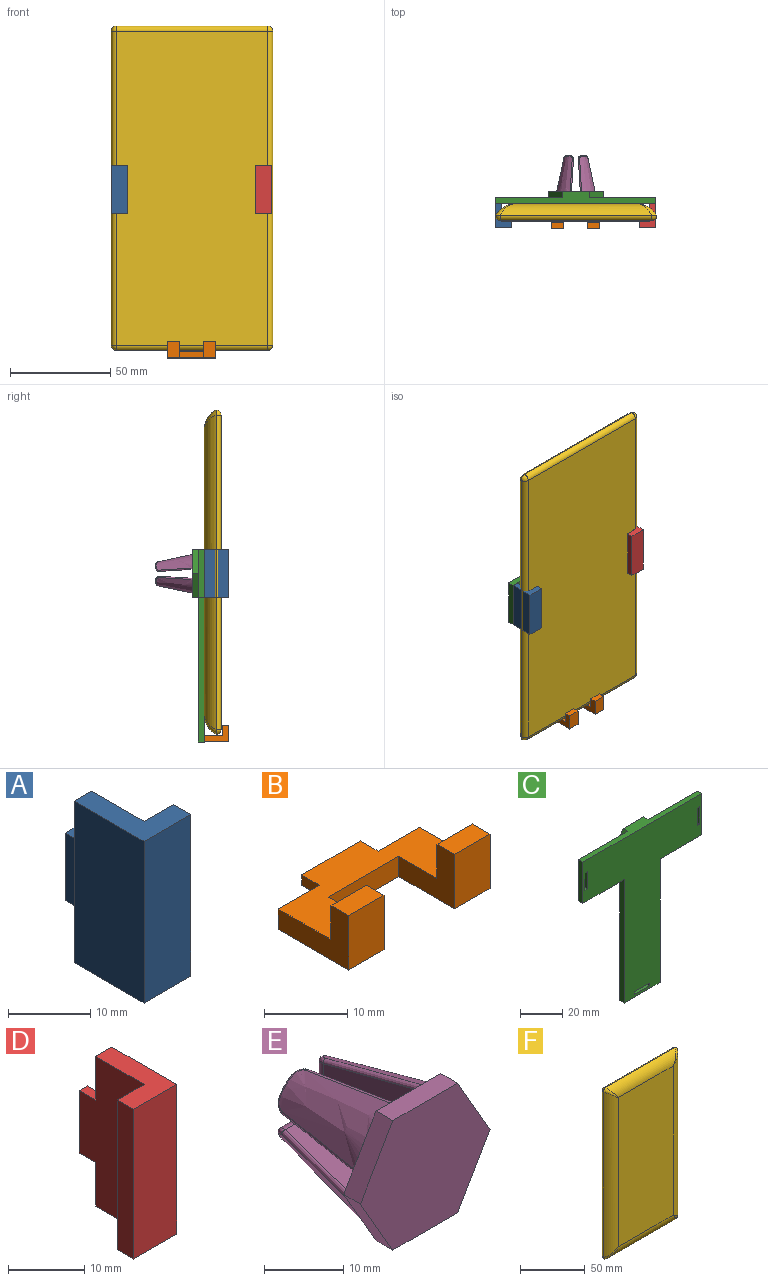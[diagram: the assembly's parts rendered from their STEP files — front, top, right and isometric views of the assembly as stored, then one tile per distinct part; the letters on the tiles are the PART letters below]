
ASSEMBLY  parts=6 mates=5
PART A: 12 faces, bbox 8x15x24 mm
  f0: plane 12x8mm, normal (0,0,-1), area 51mm2, adj f1,f4,f5,f6,f7,f11
  f1: plane 24x12mm, normal (1,0,0), area 246mm2, adj f0,f2,f3,f7,f8,f10,f11
  f2: plane 12x8mm, normal (0,0,1), area 51mm2, adj f1,f4,f5,f6,f7,f11
  f3: plane 10x1.5mm, normal (0,1,0), area 15mm2, adj f1,f8,f9,f10
  f4: plane 24x12mm, normal (-1,0,0), area 288mm2, adj f0,f2,f6,f11
  f5: plane 24x3mm, normal (1,0,0), area 72mm2, adj f0,f2,f6,f7
  f6: plane 24x8mm, normal (0,-1,0), area 192mm2, adj f0,f2,f4,f5
  f7: plane 24x5mm, normal (0,1,0), area 120mm2, adj f0,f1,f2,f5
  f8: plane 3x1.5mm, normal (0,0,1), area 4.5mm2, adj f1,f3,f9,f11
  f9: plane 10x3mm, normal (-1,0,0), area 30mm2, adj f3,f8,f10,f11
  f10: plane 3x1.5mm, normal (0,0,-1), area 4.5mm2, adj f1,f3,f9,f11
  f11: plane 24x3mm, normal (0,1,0), area 57mm2, adj f0,f1,f2,f4,f8,f9,f10
PART B: 18 faces, bbox 24x15x8 mm
  f0: plane 10x1.5mm, normal (0,1,0), area 15mm2, adj f1,f2,f3,f4
  f1: plane 24x12mm, normal (0,0,1), area 168mm2, adj f0,f3,f4,f5,f6,f7,f9,f12
  f2: plane 10x3mm, normal (0,0,-1), area 30mm2, adj f0,f3,f4,f5
  f3: plane 3x1.5mm, normal (-1,0,0), area 4.5mm2, adj f0,f1,f2,f5
  f4: plane 3x1.5mm, normal (1,0,0), area 4.5mm2, adj f0,f1,f2,f5
  f5: plane 24x3mm, normal (0,1,0), area 57mm2, adj f1,f2,f3,f4,f7,f8,f16
  f6: plane 9.5x8mm, normal (1,0,0), area 43.5mm2, adj f1,f8,f9,f10,f11,f17
  f7: plane 12x8mm, normal (-1,0,0), area 51mm2, adj f1,f5,f8,f9,f10,f11
  f8: plane 24x12mm, normal (0,0,-1), area 174mm2, adj f5,f6,f7,f11,f12,f15,f16,f17
  f9: plane 6x5mm, normal (0,1,0), area 30mm2, adj f1,f6,f7,f10
  f10: plane 6x3mm, normal (0,0,1), area 18mm2, adj f6,f7,f9,f11
  f11: plane 8x6mm, normal (0,-1,0), area 48mm2, adj f6,f7,f8,f10
  f12: plane 9.5x8mm, normal (-1,0,0), area 43.5mm2, adj f1,f8,f13,f14,f15,f17
  f13: plane 6x5mm, normal (0,1,0), area 30mm2, adj f1,f12,f14,f16
  f14: plane 6x3mm, normal (0,0,1), area 18mm2, adj f12,f13,f15,f16
  f15: plane 8x6mm, normal (0,-1,0), area 48mm2, adj f8,f12,f14,f16
  f16: plane 12x8mm, normal (1,0,0), area 51mm2, adj f1,f5,f8,f13,f14,f15
  f17: plane 12x3mm, normal (0,-1,0), area 36mm2, adj f1,f6,f8,f12
PART C: 35 faces, bbox 80x6x96 mm
  f0: plane 72x3mm, normal (-1,0,0), area 216mm2, adj f2,f3,f4,f5
  f1: plane 72x3mm, normal (1,0,0), area 216mm2, adj f2,f3,f4,f6
  f2: plane 24x3mm, normal (0,0,-1), area 72mm2, adj f0,f1,f3,f4
  f3: plane 96x80mm, normal (0,1,0), area 3100.7mm2, adj f0,f1,f2,f5,f6,f7,f8,f9
  f4: plane 96x80mm, normal (0,-1,0), area 3599.5mm2, adj f0,f1,f2,f5,f6,f7,f8,f9
  f5: plane 28x3mm, normal (0,0,-1), area 84mm2, adj f0,f3,f4,f9
  f6: plane 28x3mm, normal (0,0,-1), area 84mm2, adj f1,f3,f4,f7
  f7: plane 24x3mm, normal (1,0,0), area 72mm2, adj f3,f4,f6,f8
  f8: plane 80x6mm, normal (0,0,1), area 281.6mm2, adj f3,f4,f7,f9,f16,f17,f21
  f9: plane 24x3mm, normal (-1,0,0), area 72mm2, adj f3,f4,f5,f8
  f10: plane 10.1x5.83mm, normal (0.87,0,-0.5), area 35mm2, adj f11,f20,f21,f22
  f11: plane 10.1x5.83mm, normal (0.87,0,0.5), area 35mm2, adj f10,f12,f21,f22
  f12: plane 11.66x3mm, normal (0,0,1), area 35mm2, adj f11,f13,f21,f22
  f13: plane 10.1x5.83mm, normal (-0.87,0,0.5), area 35mm2, adj f12,f14,f21,f22
  f14: plane 10.1x5.83mm, normal (-0.87,0,-0.5), area 35mm2, adj f13,f20,f21,f22
  f15: plane 12x6.93mm, normal (-0.87,0,-0.5), area 41.6mm2, adj f3,f16,f19,f21
  f16: plane 12x6.93mm, normal (-0.87,0,0.5), area 41.6mm2, adj f3,f8,f15,f21
  f17: plane 12x6.93mm, normal (0.87,0,0.5), area 41.6mm2, adj f3,f8,f18,f21
  f18: plane 12x6.93mm, normal (0.87,0,-0.5), area 41.6mm2, adj f3,f17,f19,f21
  f19: plane 13.86x3mm, normal (0,0,-1), area 41.6mm2, adj f3,f15,f18,f21
  f20: plane 11.66x3mm, normal (0,0,-1), area 35mm2, adj f10,f14,f21,f22
  f21: plane 27.71x24mm, normal (0,1,0), area 145.5mm2, adj f8,f10,f11,f12,f13,f14,f15,f16
  f22: plane 23.33x20.2mm, normal (0,1,0), area 353.4mm2, adj f10,f11,f12,f13,f14,f20
  f23: plane 10.1x3mm, normal (1,0,0), area 30.3mm2, adj f3,f4,f24,f25
  f24: plane 3x1.6mm, normal (0,0,-1), area 4.8mm2, adj f3,f4,f23,f26
  f25: plane 3x1.6mm, normal (0,0,1), area 4.8mm2, adj f3,f4,f23,f26
  f26: plane 10.1x3mm, normal (-1,0,0), area 30.3mm2, adj f3,f4,f24,f25
  f27: plane 10.1x3mm, normal (0,0,1), area 30.3mm2, adj f3,f4,f28,f29
  f28: plane 3x1.6mm, normal (1,0,0), area 4.8mm2, adj f3,f4,f27,f30
  f29: plane 3x1.6mm, normal (-1,0,0), area 4.8mm2, adj f3,f4,f27,f30
  f30: plane 10.1x3mm, normal (0,0,-1), area 30.3mm2, adj f3,f4,f28,f29
  f31: plane 10.1x3mm, normal (1,0,0), area 30.3mm2, adj f3,f4,f32,f33
  f32: plane 3x1.6mm, normal (0,0,-1), area 4.8mm2, adj f3,f4,f31,f34
  f33: plane 3x1.6mm, normal (0,0,1), area 4.8mm2, adj f3,f4,f31,f34
  f34: plane 10.1x3mm, normal (-1,0,0), area 30.3mm2, adj f3,f4,f32,f33
PART D: 12 faces, bbox 8x15x24 mm
  f0: plane 12x8mm, normal (0,0,-1), area 51mm2, adj f1,f3,f5,f6,f7,f11
  f1: plane 24x12mm, normal (1,0,0), area 288mm2, adj f0,f4,f6,f11
  f2: plane 10x1.5mm, normal (0,1,0), area 15mm2, adj f3,f8,f9,f10
  f3: plane 24x12mm, normal (-1,0,0), area 246mm2, adj f0,f2,f4,f7,f8,f10,f11
  f4: plane 12x8mm, normal (0,0,1), area 51mm2, adj f1,f3,f5,f6,f7,f11
  f5: plane 24x3mm, normal (-1,0,0), area 72mm2, adj f0,f4,f6,f7
  f6: plane 24x8mm, normal (0,-1,0), area 192mm2, adj f0,f1,f4,f5
  f7: plane 24x5mm, normal (0,1,0), area 120mm2, adj f0,f3,f4,f5
  f8: plane 3x1.5mm, normal (0,0,-1), area 4.5mm2, adj f2,f3,f9,f11
  f9: plane 10x3mm, normal (1,0,0), area 30mm2, adj f2,f8,f10,f11
  f10: plane 3x1.5mm, normal (0,0,1), area 4.5mm2, adj f2,f3,f9,f11
  f11: plane 24x3mm, normal (0,1,0), area 57mm2, adj f0,f1,f3,f4,f8,f9,f10
PART E: 60 faces, bbox 23.2x23.4x20.6 mm
  f0: bspline ~17.61x8.03mm, area 141.2mm2, adj f4,f18,f19,f20,f48,f52
  f1: bspline ~17.61x8.03mm, area 141.2mm2, adj f4,f22,f23,f24,f43,f47
  f2: bspline ~17.61x8.03mm, area 141.2mm2, adj f4,f26,f27,f28,f38,f42
  f3: bspline ~17.61x8.03mm, area 141.2mm2, adj f4,f30,f31,f32,f33,f37
  f4: plane 23.16x20.06mm, normal (0,1,0), area 188.5mm2, adj f0,f1,f2,f3,f6,f7,f9,f10
  f5: plane 2.21x2.21mm, normal (0,1,0), area 2.9mm2, adj f31,f34,f36
  f6: plane 16.41x7.38mm, normal (-1,-0.06,0), area 84.4mm2, adj f4,f29,f32,f34
  f7: plane 16.41x7.38mm, normal (0,-0.06,-1), area 84.4mm2, adj f4,f29,f30,f36
  f8: plane 2.21x2.21mm, normal (0,1,0), area 2.9mm2, adj f27,f39,f41
  f9: plane 16.41x7.38mm, normal (1,-0.06,0), area 84.4mm2, adj f4,f25,f28,f39
  f10: plane 16.41x7.38mm, normal (0,-0.06,-1), area 84.4mm2, adj f4,f25,f26,f41
  f11: plane 2.21x2.21mm, normal (0,1,0), area 2.9mm2, adj f23,f44,f46
  f12: plane 16.41x7.38mm, normal (-1,-0.06,0), area 84.4mm2, adj f4,f21,f24,f44
  f13: plane 16.41x7.38mm, normal (0,-0.06,1), area 84.4mm2, adj f4,f21,f22,f46
  f14: plane 2.21x2.21mm, normal (0,1,0), area 2.9mm2, adj f19,f49,f51
  f15: plane 16.41x7.38mm, normal (0,-0.06,1), area 84.4mm2, adj f4,f17,f20,f49
  f16: plane 16.41x7.38mm, normal (1,-0.06,0), area 84.4mm2, adj f4,f17,f18,f51
  f17: cylinder r=0.5mm len=16.42mm, axis (-0.06,-1,-0.06), area 12.9mm2, adj f4,f15,f16,f50
  f18: bspline ~22.76x5.5mm, area 15.8mm2, adj f0,f4,f16,f52
  f19: bspline ~3.66x3.46mm, area 2.2mm2, adj f0,f14,f48,f52
  f20: bspline ~22.76x5.5mm, area 15.8mm2, adj f0,f4,f15,f48
  f21: cylinder r=0.5mm len=16.42mm, axis (0.06,-1,-0.06), area 12.9mm2, adj f4,f12,f13,f45
  f22: bspline ~22.76x5.5mm, area 15.8mm2, adj f1,f4,f13,f47
  f23: bspline ~3.66x3.46mm, area 2.2mm2, adj f1,f11,f43,f47
  f24: bspline ~22.76x5.5mm, area 15.8mm2, adj f1,f4,f12,f43
  f25: cylinder r=0.5mm len=16.42mm, axis (-0.06,-1,0.06), area 12.9mm2, adj f4,f9,f10,f40
  f26: bspline ~22.76x5.5mm, area 15.8mm2, adj f2,f4,f10,f42
  f27: bspline ~3.66x3.46mm, area 2.2mm2, adj f2,f8,f38,f42
  f28: bspline ~22.76x5.5mm, area 15.8mm2, adj f2,f4,f9,f38
  f29: cylinder r=0.5mm len=16.42mm, axis (-0.06,1,-0.06), area 12.9mm2, adj f4,f6,f7,f35
  f30: bspline ~20.19x4.95mm, area 15.8mm2, adj f3,f4,f7,f37
  f31: bspline ~3.66x3.46mm, area 2.2mm2, adj f3,f5,f33,f37
  f32: bspline ~20.19x4.95mm, area 15.8mm2, adj f3,f4,f6,f33
  f33: bspline ~2.04x1.76mm, area 1.9mm2, adj f3,f31,f32,f34
  f34: cylinder r=1.5mm len=3.87mm, axis (0,0,-1), area 7.4mm2, adj f5,f6,f33,f35
  f35: bspline ~1.76x1.5mm, area 0.9mm2, adj f29,f34,f36
  f36: cylinder r=1.5mm len=3.87mm, axis (-1,0,0), area 7.4mm2, adj f5,f7,f35,f37
  f37: bspline ~1.92x1.83mm, area 1.9mm2, adj f3,f30,f31,f36
  f38: bspline ~1.92x1.83mm, area 1.9mm2, adj f2,f27,f28,f39
  f39: cylinder r=1.5mm len=3.87mm, axis (0,0,-1), area 7.4mm2, adj f8,f9,f38,f40
  f40: bspline ~1.76x1.5mm, area 0.9mm2, adj f25,f39,f41
  f41: cylinder r=1.5mm len=3.87mm, axis (1,0,0), area 7.4mm2, adj f8,f10,f40,f42
  f42: bspline ~2.04x1.76mm, area 1.9mm2, adj f2,f26,f27,f41
  f43: bspline ~1.92x1.83mm, area 1.9mm2, adj f1,f23,f24,f44
  f44: cylinder r=1.5mm len=3.87mm, axis (0,0,1), area 7.4mm2, adj f11,f12,f43,f45
  f45: bspline ~1.76x1.5mm, area 0.9mm2, adj f21,f44,f46
  f46: cylinder r=1.5mm len=3.87mm, axis (-1,0,0), area 7.4mm2, adj f11,f13,f45,f47
  f47: bspline ~2.04x1.76mm, area 1.9mm2, adj f1,f22,f23,f46
  f48: bspline ~1.92x1.83mm, area 1.9mm2, adj f0,f19,f20,f49
  f49: cylinder r=1.5mm len=3.87mm, axis (1,0,0), area 7.4mm2, adj f14,f15,f48,f50
  f50: bspline ~1.76x1.5mm, area 0.9mm2, adj f17,f49,f51
  f51: cylinder r=1.5mm len=3.87mm, axis (0,0,1), area 7.4mm2, adj f14,f16,f50,f52
  f52: bspline ~2.04x1.76mm, area 1.9mm2, adj f0,f18,f19,f51
  f53: plane 11.55x3mm, normal (0,0,1), area 34.6mm2, adj f4,f54,f58,f59
  f54: plane 10x5.77mm, normal (0.87,0,0.5), area 34.6mm2, adj f4,f53,f55,f59
  f55: plane 10x5.77mm, normal (0.87,0,-0.5), area 34.6mm2, adj f4,f54,f56,f59
  f56: plane 11.55x3mm, normal (0,0,-1), area 34.6mm2, adj f4,f55,f57,f59
  f57: plane 10x5.77mm, normal (-0.87,0,-0.5), area 34.6mm2, adj f4,f56,f58,f59
  f58: plane 10x5.77mm, normal (-0.87,0,0.5), area 34.6mm2, adj f4,f53,f57,f59
  f59: plane 23.09x20mm, normal (0,-1,0), area 346.4mm2, adj f53,f54,f55,f56,f57,f58
PART F: 18 faces, bbox 80.6x8.5x162 mm
  f0: plane 141.22x59.82mm, normal (0,-1,0), area 8446.9mm2, adj f10,f13,f14,f17
  f1: plane 157x75.6mm, normal (0,1,0), area 11869.2mm2, adj f3,f4,f7,f8
  f2: sphere r=2.5mm, area 9.8mm2, adj f3,f4,f11
  f3: cylinder r=2.5mm len=75.6mm, axis (-1,0,0), area 296.9mm2, adj f1,f2,f5,f13
  f4: cylinder r=2.5mm len=157mm, axis (0,0,-1), area 616.5mm2, adj f1,f2,f6,f10
  f5: sphere r=2.5mm, area 13.4mm2, adj f3,f7,f15
  f6: sphere r=2.5mm, area 9.8mm2, adj f4,f8,f12
  f7: cylinder r=2.5mm len=157mm, axis (0,0,1), area 616.5mm2, adj f1,f5,f9,f17
  f8: cylinder r=2.5mm len=75.6mm, axis (1,0,0), area 296.9mm2, adj f1,f6,f9,f14
  f9: sphere r=2.5mm, area 6.2mm2, adj f7,f8,f16
  f10: cylinder r=12mm len=157mm, axis (0,0,-1), area 1873.7mm2, adj f0,f4,f11,f12
  f11: bspline ~10.39x10.39mm, area 20mm2, adj f2,f10,f13
  f12: bspline ~10.39x10.39mm, area 20mm2, adj f6,f10,f14
  f13: cylinder r=12mm len=75.6mm, axis (1,0,0), area 850.8mm2, adj f0,f3,f11,f15
  f14: cylinder r=12mm len=75.6mm, axis (1,0,0), area 850.8mm2, adj f0,f8,f12,f16
  f15: bspline ~10.39x10.39mm, area 20mm2, adj f5,f13,f17
  f16: bspline ~10.39x10.39mm, area 20mm2, adj f9,f14,f17
  f17: cylinder r=12mm len=157mm, axis (0,0,-1), area 1873.7mm2, adj f0,f7,f15,f16
PLACE A t=(-81.2,-40.39,27.55)mm
PLACE B t=(-94.2,-40.39,40.65)mm
PLACE C t=(-94.2,-40.39,27.55)mm
PLACE D t=(-107.2,-40.39,27.55)mm
PLACE E t=(-94.2,-57.39,27.55)mm
PLACE F rot(axis=(1,0,0),180deg) t=(-237.27,-68.89,1.55)mm
MATE fastened B.f0 <-> C.f3  axis (0,1,0) through (-94.2,-57.39,-53.35)mm
MATE fastened E.f59 <-> C.f22  axis (0,-1,0) through (-94.2,-57.39,27.55)mm
MATE planar C.f4 <-> F.f0  axis (0,-1,0) through (-94.2,-60.39,4.88)mm
MATE fastened D.f2 <-> C.f3  axis (0,1,0) through (-55.7,-57.39,27.55)mm
MATE fastened A.f3 <-> C.f3  axis (0,1,0) through (-132.7,-57.39,27.55)mm
